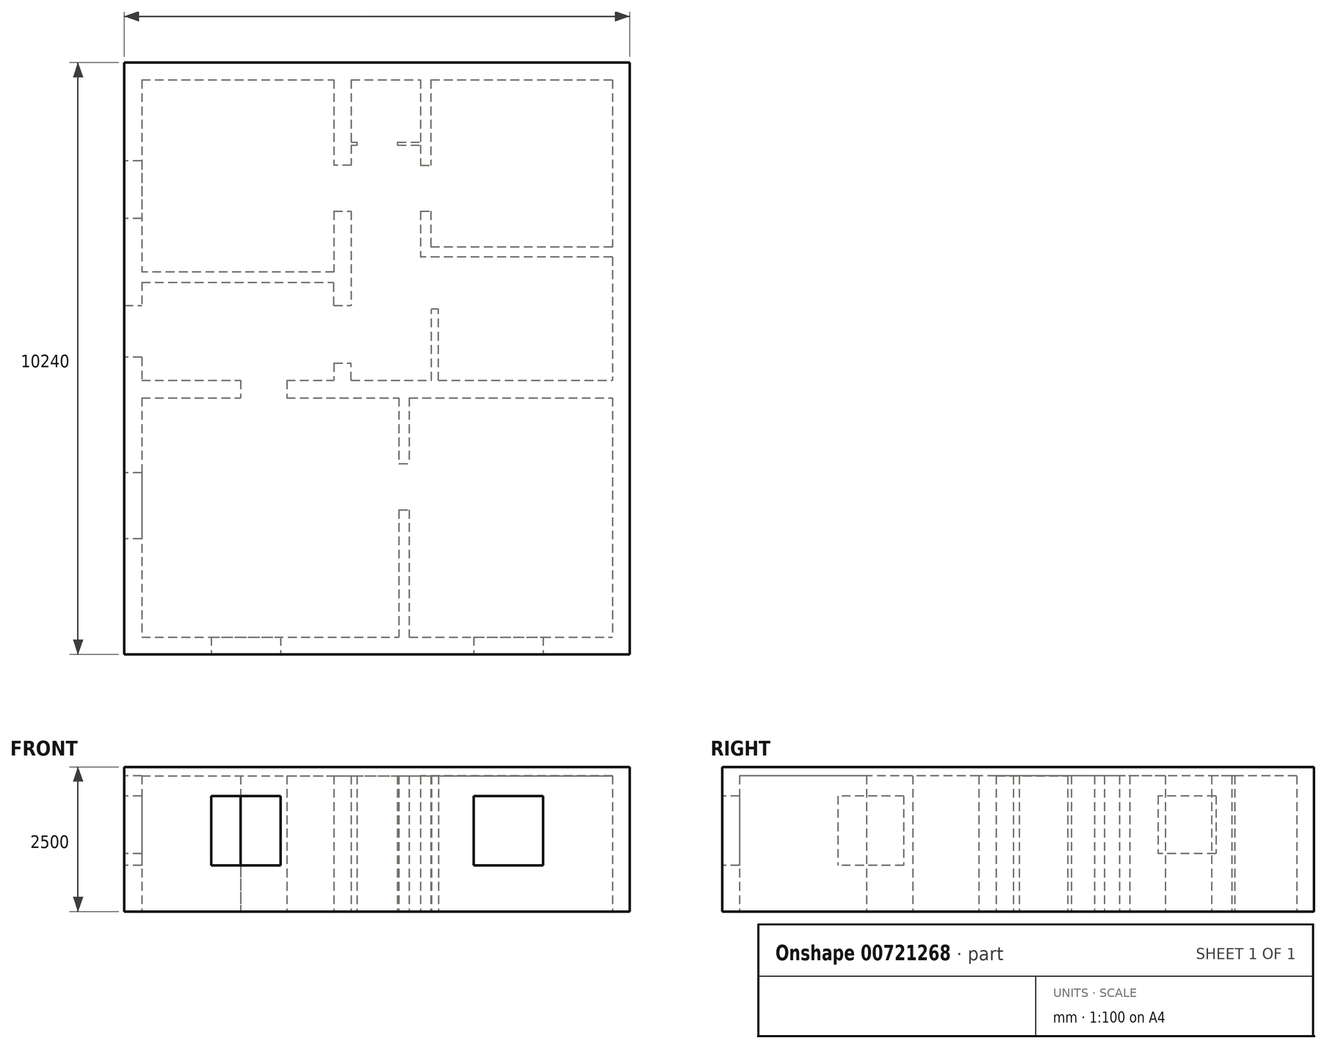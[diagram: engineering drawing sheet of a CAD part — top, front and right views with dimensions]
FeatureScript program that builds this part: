
annotation { "Feature Type Name" : "Feature", "Feature Type Description" : "" }
export const myFeature = defineFeature(function(context is Context, id is Id, definition is map)
    precondition{}
    {
        {
            var Q0;
            Q0=qCreatedBy(makeId("Top.planeOp"),FACE);
            var sketch = newSketch(context, id + "F0", { "sketchPlane" : qUnion([Q0])});
            skLineSegment(sketch, "E0.bottom", {"start": v(-2880.1, 3953.48) * mm, "end": v(5859.9, 3953.48) * mm});
            skLineSegment(sketch, "E0.top", {"start": v(-2880.1, -6286.52) * mm, "end": v(5859.9, -6286.52) * mm});
            skLineSegment(sketch, "E0.left", {"start": v(-2880.1, 3953.48) * mm, "end": v(-2880.1, -246.52) * mm});
            skLineSegment(sketch, "E0.right", {"start": v(5859.9, 3953.48) * mm, "end": v(5859.9, -6286.52) * mm});
            skLineSegment(sketch, "E1.bottom", {"start": v(-2580.1, 3653.48) * mm, "end": v(744.9, 3653.48) * mm});
            skLineSegment(sketch, "E1.top", {"start": v(-2580.1, -5986.52) * mm, "end": v(1869.9, -5986.52) * mm});
            skLineSegment(sketch, "E1.left", {"start": v(-2580.1, 3653.48) * mm, "end": v(-2580.1, 328.48) * mm});
            skLineSegment(sketch, "E1.right", {"start": v(5559.9, 3653.48) * mm, "end": v(5559.9, 763.48) * mm});
            skLineSegment(sketch, "E2", {"start": v(-2580.1, -1546.52) * mm, "end": v(-872.6, -1546.52) * mm});
            skLineSegment(sketch, "E3", {"start": v(-2580.1, -1846.52) * mm, "end": v(-872.6, -1846.52) * mm});
            skLineSegment(sketch, "E4", {"start": v(744.9, 3653.48) * mm, "end": v(744.9, 2180.1) * mm});
            skLineSegment(sketch, "E5", {"start": v(744.9, 328.48) * mm, "end": v(-2580.1, 328.48) * mm});
            skLineSegment(sketch, "E6", {"start": v(2419.9, 3653.48) * mm, "end": v(2419.9, 2180.1) * mm});
            skLineSegment(sketch, "E7", {"start": v(5559.9, 763.48) * mm, "end": v(2419.9, 763.48) * mm});
            skLineSegment(sketch, "E8", {"start": v(2044.9, -1846.52) * mm, "end": v(2044.9, -2986.52) * mm});
            skLineSegment(sketch, "E9", {"start": v(1869.9, -1846.52) * mm, "end": v(1869.9, -2986.52) * mm});
            skLineSegment(sketch, "E10", {"start": v(-2580.1, 153.48) * mm, "end": v(744.9, 153.48) * mm});
            skLineSegment(sketch, "E11", {"start": v(1044.9, 3653.48) * mm, "end": v(1044.9, 2578.48) * mm});
            skLineSegment(sketch, "E12", {"start": v(2244.9, 3653.48) * mm, "end": v(2244.9, 2578.48) * mm});
            skLineSegment(sketch, "E13", {"start": v(5559.9, 588.48) * mm, "end": v(2244.9, 588.48) * mm});
            skLineSegment(sketch, "E14", {"start": v(2549.9, -1546.52) * mm, "end": v(2549.9, -311.52) * mm});
            skLineSegment(sketch, "E15", {"start": v(744.9, -246.52) * mm, "end": v(1044.9, -246.52) * mm});
            skLineSegment(sketch, "E16", {"start": v(744.9, -246.52) * mm, "end": v(744.9, 153.48) * mm});
            skLineSegment(sketch, "E17", {"start": v(2549.9, -311.52) * mm, "end": v(2434.9, -311.52) * mm});
            skLineSegment(sketch, "E18", {"start": v(2434.9, -1546.52) * mm, "end": v(2434.9, -311.52) * mm});
            skLineSegment(sketch, "E19", {"start": v(1044.9, 2578.48) * mm, "end": v(1144.9, 2578.48) * mm});
            skLineSegment(sketch, "E20", {"start": v(1044.9, 2528.48) * mm, "end": v(1144.9, 2528.48) * mm});
            skLineSegment(sketch, "E21.trimOffspring", {"start": v(1044.9, 2528.48) * mm, "end": v(1044.9, 2180.1) * mm});
            skLineSegment(sketch, "E22.trimOffspring", {"start": v(2244.9, 2528.48) * mm, "end": v(2244.9, 2180.1) * mm});
            skLineSegment(sketch, "E23.trimOffspring", {"start": v(1044.9, 3653.48) * mm, "end": v(2244.9, 3653.48) * mm});
            skLineSegment(sketch, "E24.trimOffspring", {"start": v(2419.9, 3653.48) * mm, "end": v(5559.9, 3653.48) * mm});
            skLineSegment(sketch, "E25.trimOffspring", {"start": v(2549.9, -1546.52) * mm, "end": v(5559.9, -1546.52) * mm});
            skLineSegment(sketch, "E26.trimOffspring", {"start": v(5559.9, 588.48) * mm, "end": v(5559.9, -1546.52) * mm});
            skLineSegment(sketch, "E27.trimOffspring", {"start": v(2044.9, -1846.52) * mm, "end": v(5559.9, -1846.52) * mm});
            skLineSegment(sketch, "E28.trimOffspring", {"start": v(2044.9, -5986.52) * mm, "end": v(5559.9, -5986.52) * mm});
            skLineSegment(sketch, "E29.trimOffspring", {"start": v(-2580.1, -1846.52) * mm, "end": v(-2580.1, -5986.52) * mm});
            skLineSegment(sketch, "E30.trimOffspring", {"start": v(-2580.1, 153.48) * mm, "end": v(-2580.1, -246.52) * mm});
            skLineSegment(sketch, "E31", {"start": v(-72.6, -1546.52) * mm, "end": v(-72.6, -1846.52) * mm});
            skLineSegment(sketch, "E32", {"start": v(-872.6, -1546.52) * mm, "end": v(-872.6, -1846.52) * mm});
            skLineSegment(sketch, "E33.trimOffspring", {"start": v(-72.6, -1546.52) * mm, "end": v(744.9, -1546.52) * mm});
            skLineSegment(sketch, "E34.trimOffspring", {"start": v(-72.6, -1846.52) * mm, "end": v(1869.9, -1846.52) * mm});
            skLineSegment(sketch, "E35", {"start": v(1144.9, 2578.48) * mm, "end": v(1144.9, 2528.48) * mm});
            skLineSegment(sketch, "E36", {"start": v(1844.9, 2578.48) * mm, "end": v(1844.9, 2528.48) * mm});
            skLineSegment(sketch, "E37.trimOffspring", {"start": v(1844.9, 2578.48) * mm, "end": v(2244.9, 2578.48) * mm});
            skLineSegment(sketch, "E38.trimOffspring", {"start": v(1844.9, 2528.48) * mm, "end": v(2244.9, 2528.48) * mm});
            skLineSegment(sketch, "E39", {"start": v(1044.9, 2180.1) * mm, "end": v(744.9, 2180.1) * mm});
            skLineSegment(sketch, "E40", {"start": v(744.9, 1380.1) * mm, "end": v(1044.9, 1380.1) * mm});
            skLineSegment(sketch, "E41.trimOffspring", {"start": v(744.9, 1380.1) * mm, "end": v(744.9, 328.48) * mm});
            skLineSegment(sketch, "E42", {"start": v(1044.9, 1380.1) * mm, "end": v(1044.9, -246.52) * mm});
            skLineSegment(sketch, "E43", {"start": v(1869.9, -2986.52) * mm, "end": v(2044.9, -2986.52) * mm});
            skLineSegment(sketch, "E44", {"start": v(1869.9, -3786.52) * mm, "end": v(2044.9, -3786.52) * mm});
            skLineSegment(sketch, "E45.trimOffspring", {"start": v(2044.9, -3786.52) * mm, "end": v(2044.9, -5986.52) * mm});
            skLineSegment(sketch, "E46.trimOffspring", {"start": v(1869.9, -3786.52) * mm, "end": v(1869.9, -5986.52) * mm});
            skLineSegment(sketch, "E47", {"start": v(-2880.1, -246.52) * mm, "end": v(-2580.1, -246.52) * mm});
            skLineSegment(sketch, "E48", {"start": v(-2580.1, -1146.52) * mm, "end": v(-2880.1, -1146.52) * mm});
            skLineSegment(sketch, "E49.trimOffspring", {"start": v(-2880.1, -1146.52) * mm, "end": v(-2880.1, -6286.52) * mm});
            skLineSegment(sketch, "E50.trimOffspring", {"start": v(-2580.1, -1146.52) * mm, "end": v(-2580.1, -1546.52) * mm});
            skLineSegment(sketch, "E51", {"start": v(2244.9, 2180.1) * mm, "end": v(2419.9, 2180.1) * mm});
            skLineSegment(sketch, "E52", {"start": v(2244.9, 1380.1) * mm, "end": v(2419.9, 1380.1) * mm});
            skLineSegment(sketch, "E53.trimOffspring", {"start": v(2244.9, 1380.1) * mm, "end": v(2244.9, 588.48) * mm});
            skLineSegment(sketch, "E54.trimOffspring", {"start": v(2419.9, 1380.1) * mm, "end": v(2419.9, 763.48) * mm});
            skLineSegment(sketch, "E55", {"start": v(744.9, -1246.52) * mm, "end": v(744.9, -1546.52) * mm});
            skLineSegment(sketch, "E56", {"start": v(744.9, -1246.52) * mm, "end": v(1044.9, -1246.52) * mm});
            skLineSegment(sketch, "E57", {"start": v(1044.9, -1546.52) * mm, "end": v(1044.9, -1246.52) * mm});
            skLineSegment(sketch, "E58.trimOffspring", {"start": v(1044.9, -1546.52) * mm, "end": v(2434.9, -1546.52) * mm});
            skLineSegment(sketch, "E59.trimOffspring", {"start": v(5559.9, -1846.52) * mm, "end": v(5559.9, -5986.52) * mm});
            skSolve(sketch);
        }
        {
            var Q0;
            Q0=makeQuery(id+"F0.imprint","IMPRINT",FACE,{"disambiguationData":[TD([[makeQuery(id+"F0.imprint","IMPRINT",EDGE,{"derivedFrom":sQuery(id+"F0.wireOp",EDGE,"E0.bottom")}),-1.0]])]});
            extrude(context, id + "F1", {"entities" : qUnion([Q0]), "depth" : 2350 * mm, "offsetDistance" : 25 * mm});
        }
        {
            var Q0;
            Q0=makeQuery(id+"F1.opExtrude","CAP_FACE",FACE,{"disambiguationData":[OSD([sQuery(id+"F0.wireOp",EDGE,"E0.bottom"),sQuery(id+"F0.wireOp",EDGE,"E0.top"),sQuery(id+"F0.wireOp",EDGE,"E0.left"),sQuery(id+"F0.wireOp",EDGE,"E0.right"),sQuery(id+"F0.wireOp",EDGE,"E1.bottom"),sQuery(id+"F0.wireOp",EDGE,"E1.top"),sQuery(id+"F0.wireOp",EDGE,"E1.left"),sQuery(id+"F0.wireOp",EDGE,"E1.right"),sQuery(id+"F0.wireOp",EDGE,"E2"),sQuery(id+"F0.wireOp",EDGE,"E3"),sQuery(id+"F0.wireOp",EDGE,"E4"),sQuery(id+"F0.wireOp",EDGE,"E5"),sQuery(id+"F0.wireOp",EDGE,"E6"),sQuery(id+"F0.wireOp",EDGE,"E7"),sQuery(id+"F0.wireOp",EDGE,"E8"),sQuery(id+"F0.wireOp",EDGE,"E9"),sQuery(id+"F0.wireOp",EDGE,"E10"),sQuery(id+"F0.wireOp",EDGE,"E11"),sQuery(id+"F0.wireOp",EDGE,"E12"),sQuery(id+"F0.wireOp",EDGE,"E13"),sQuery(id+"F0.wireOp",EDGE,"E14"),sQuery(id+"F0.wireOp",EDGE,"E15"),sQuery(id+"F0.wireOp",EDGE,"E16"),sQuery(id+"F0.wireOp",EDGE,"E17"),sQuery(id+"F0.wireOp",EDGE,"E18"),sQuery(id+"F0.wireOp",EDGE,"E19"),sQuery(id+"F0.wireOp",EDGE,"E20"),sQuery(id+"F0.wireOp",EDGE,"E21.trimOffspring"),sQuery(id+"F0.wireOp",EDGE,"E22.trimOffspring"),sQuery(id+"F0.wireOp",EDGE,"E23.trimOffspring"),sQuery(id+"F0.wireOp",EDGE,"E24.trimOffspring"),sQuery(id+"F0.wireOp",EDGE,"E25.trimOffspring"),sQuery(id+"F0.wireOp",EDGE,"E26.trimOffspring"),sQuery(id+"F0.wireOp",EDGE,"E27.trimOffspring"),sQuery(id+"F0.wireOp",EDGE,"E28.trimOffspring"),sQuery(id+"F0.wireOp",EDGE,"E29.trimOffspring"),sQuery(id+"F0.wireOp",EDGE,"E30.trimOffspring"),sQuery(id+"F0.wireOp",EDGE,"E31"),sQuery(id+"F0.wireOp",EDGE,"E32"),sQuery(id+"F0.wireOp",EDGE,"E33.trimOffspring"),sQuery(id+"F0.wireOp",EDGE,"E34.trimOffspring"),sQuery(id+"F0.wireOp",EDGE,"E35"),sQuery(id+"F0.wireOp",EDGE,"E36"),sQuery(id+"F0.wireOp",EDGE,"E37.trimOffspring"),sQuery(id+"F0.wireOp",EDGE,"E38.trimOffspring"),sQuery(id+"F0.wireOp",EDGE,"E39"),sQuery(id+"F0.wireOp",EDGE,"E40"),sQuery(id+"F0.wireOp",EDGE,"E41.trimOffspring"),sQuery(id+"F0.wireOp",EDGE,"E42"),sQuery(id+"F0.wireOp",EDGE,"E43"),sQuery(id+"F0.wireOp",EDGE,"E44"),sQuery(id+"F0.wireOp",EDGE,"E45.trimOffspring"),sQuery(id+"F0.wireOp",EDGE,"E46.trimOffspring"),sQuery(id+"F0.wireOp",EDGE,"E47"),sQuery(id+"F0.wireOp",EDGE,"E48"),sQuery(id+"F0.wireOp",EDGE,"E49.trimOffspring"),sQuery(id+"F0.wireOp",EDGE,"E50.trimOffspring"),sQuery(id+"F0.wireOp",EDGE,"E51"),sQuery(id+"F0.wireOp",EDGE,"E52"),sQuery(id+"F0.wireOp",EDGE,"E53.trimOffspring"),sQuery(id+"F0.wireOp",EDGE,"E54.trimOffspring"),sQuery(id+"F0.wireOp",EDGE,"E55"),sQuery(id+"F0.wireOp",EDGE,"E56"),sQuery(id+"F0.wireOp",EDGE,"E57"),sQuery(id+"F0.wireOp",EDGE,"E58.trimOffspring"),sQuery(id+"F0.wireOp",EDGE,"E59.trimOffspring")])],"isStart":false});
            var sketch = newSketch(context, id + "F2", { "sketchPlane" : qUnion([Q0])});
            skLineSegment(sketch, "E60.bottom", {"start": v(-2880.1, 3953.48) * mm, "end": v(5859.9, 3953.48) * mm});
            skLineSegment(sketch, "E60.top", {"start": v(-2880.1, -6286.52) * mm, "end": v(5859.9, -6286.52) * mm});
            skLineSegment(sketch, "E60.left", {"start": v(-2880.1, 3953.48) * mm, "end": v(-2880.1, -6286.52) * mm});
            skLineSegment(sketch, "E60.right", {"start": v(5859.9, 3953.48) * mm, "end": v(5859.9, -6286.52) * mm});
            skSolve(sketch);
        }
        {
            var Q0;
            Q0 = qSketchRegion(id + "F2", true);
            extrude(context, id + "F3", {"entities" : qUnion([Q0]), "operationType" : NewBodyOperationType.ADD, "depth" : 150 * mm, "offsetDistance" : 25 * mm});
        }
        {
            var Q0;
            Q0=makeQuery(id+"F3.boolean.opBoolean","MERGE",FACE,{"derivedFrom":[makeQuery(id+"F1.opExtrude","SWEPT_FACE",FACE,{"disambiguationData":[OSD([sQuery(id+"F0.wireOp",EDGE,"E0.left")])]}),makeQuery(id+"F1.opExtrude","SWEPT_FACE",FACE,{"disambiguationData":[OSD([sQuery(id+"F0.wireOp",EDGE,"E49.trimOffspring")])]}),makeQuery(id+"F3.opExtrude","SWEPT_FACE",FACE,{"disambiguationData":[OSD([sQuery(id+"F2.wireOp",EDGE,"E60.left")])]})]});
            var sketch = newSketch(context, id + "F4", { "sketchPlane" : qUnion([Q0])});
            skLineSegment(sketch, "E61.bottom", {"start": v(-2253.48, 2000) * mm, "end": v(-1253.48, 2000) * mm});
            skLineSegment(sketch, "E61.top", {"start": v(-2253.48, 1000) * mm, "end": v(-1253.48, 1000) * mm});
            skLineSegment(sketch, "E61.left", {"start": v(-2253.48, 2000) * mm, "end": v(-2253.48, 1000) * mm});
            skLineSegment(sketch, "E61.right", {"start": v(-1253.48, 2000) * mm, "end": v(-1253.48, 1000) * mm});
            skLineSegment(sketch, "E62.bottom", {"start": v(4281.26, 6877.69) * mm, "end": v(5885.44, 6877.69) * mm});
            skLineSegment(sketch, "E62.top", {"start": v(4281.26, 5959.06) * mm, "end": v(5885.44, 5959.06) * mm});
            skLineSegment(sketch, "E62.left", {"start": v(4281.26, 6877.69) * mm, "end": v(4281.26, 5959.06) * mm});
            skLineSegment(sketch, "E62.right", {"start": v(5885.44, 6877.69) * mm, "end": v(5885.44, 5959.06) * mm});
            skLineSegment(sketch, "E63.bottom", {"start": v(3146.52, 2000) * mm, "end": v(4286.52, 2000) * mm});
            skLineSegment(sketch, "E63.top", {"start": v(3146.52, 800) * mm, "end": v(4286.52, 800) * mm});
            skLineSegment(sketch, "E63.left", {"start": v(3146.52, 2000) * mm, "end": v(3146.52, 800) * mm});
            skLineSegment(sketch, "E63.right", {"start": v(4286.52, 2000) * mm, "end": v(4286.52, 800) * mm});
            skSolve(sketch);
        }
        {
            var Q0;
            Q0=makeQuery(id+"F4.imprint","IMPRINT",FACE,{"disambiguationData":[TD([[makeQuery(id+"F4.imprint","IMPRINT",EDGE,{"derivedFrom":sQuery(id+"F4.wireOp",EDGE,"E61.bottom")}),-1.0]])]});
            var Q1;
            Q1=makeQuery(id+"F4.imprint","IMPRINT",FACE,{"disambiguationData":[TD([[makeQuery(id+"F4.imprint","IMPRINT",EDGE,{"derivedFrom":sQuery(id+"F4.wireOp",EDGE,"E63.bottom")}),-1.0]])]});
            extrude(context, id + "F5", {"entities" : qUnion([Q0, Q1]), "operationType" : NewBodyOperationType.REMOVE, "oppositeDirection" : true, "depth" : 300 * mm, "offsetDistance" : 25 * mm});
        }
        {
            var Q0;
            Q0=makeQuery(id+"F3.boolean.opBoolean","MERGE",FACE,{"derivedFrom":[makeQuery(id+"F1.opExtrude","SWEPT_FACE",FACE,{"disambiguationData":[OSD([sQuery(id+"F0.wireOp",EDGE,"E0.top")])]}),makeQuery(id+"F3.opExtrude","SWEPT_FACE",FACE,{"disambiguationData":[OSD([sQuery(id+"F2.wireOp",EDGE,"E60.top")])]})]});
            var sketch = newSketch(context, id + "F6", { "sketchPlane" : qUnion([Q0])});
            skLineSegment(sketch, "E64.bottom", {"start": v(-1380.1, 2000) * mm, "end": v(-180.1, 2000) * mm});
            skLineSegment(sketch, "E64.top", {"start": v(-1380.1, 800) * mm, "end": v(-180.1, 800) * mm});
            skLineSegment(sketch, "E64.left", {"start": v(-1380.1, 2000) * mm, "end": v(-1380.1, 800) * mm});
            skLineSegment(sketch, "E64.right", {"start": v(-180.1, 2000) * mm, "end": v(-180.1, 800) * mm});
            skLineSegment(sketch, "E65.bottom", {"start": v(3159.9, 2000) * mm, "end": v(4359.9, 2000) * mm});
            skLineSegment(sketch, "E65.top", {"start": v(3159.9, 800) * mm, "end": v(4359.9, 800) * mm});
            skLineSegment(sketch, "E65.left", {"start": v(3159.9, 2000) * mm, "end": v(3159.9, 800) * mm});
            skLineSegment(sketch, "E65.right", {"start": v(4359.9, 2000) * mm, "end": v(4359.9, 800) * mm});
            skSolve(sketch);
        }
        {
            var Q0;
            Q0=makeQuery(id+"F6.imprint","IMPRINT",FACE,{"disambiguationData":[TD([[makeQuery(id+"F6.imprint","IMPRINT",EDGE,{"derivedFrom":sQuery(id+"F6.wireOp",EDGE,"E64.bottom")}),-1.0]])]});
            var Q1;
            Q1=makeQuery(id+"F6.imprint","IMPRINT",FACE,{"disambiguationData":[TD([[makeQuery(id+"F6.imprint","IMPRINT",EDGE,{"derivedFrom":sQuery(id+"F6.wireOp",EDGE,"E65.bottom")}),-1.0]])]});
            extrude(context, id + "F7", {"entities" : qUnion([Q0, Q1]), "operationType" : NewBodyOperationType.REMOVE, "oppositeDirection" : true, "depth" : 300 * mm, "offsetDistance" : 25 * mm});
        }
    });
